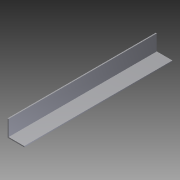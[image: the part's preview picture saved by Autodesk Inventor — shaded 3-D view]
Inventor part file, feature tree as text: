
AUTODESK INVENTOR PART (.ipt)
format: ipt  version: 2012 (Build 160160000, 160)  size: 74,240 bytes
history: native  units: in
note: dims shown in document units (in); Inventor stores cm internally (conversion verified against a paired STEP export)
features: extrude x1, sketch x1
ambient origin geometry x8: Origin, YZ Plane, XZ Plane, XY Plane, X Axis, Y Axis, Z Axis, Center Point
bodies: Solid1 (feature_tree)
feature tree (2):
  extrude  "Extrusion1"  Depth=0.0625in
  sketch  "Sketch1"  dims[d0=0.0625in d1=0.0625in d2=1.0in d3=1.0in d4=8.875in d5=0.0in]
